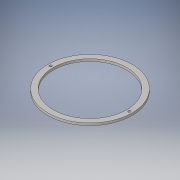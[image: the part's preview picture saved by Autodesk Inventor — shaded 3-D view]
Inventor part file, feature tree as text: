
AUTODESK INVENTOR PART (.ipt)
format: ipt  version: 2016 (Build 200138000, 138)  size: 108,032 bytes
history: native  units: in
note: dims shown in document units (in); Inventor stores cm internally (conversion verified against a paired STEP export)
features: extrude x2, sketch x2
ambient origin geometry x8: Origin, YZ Plane, XZ Plane, XY Plane, X Axis, Y Axis, Z Axis, Center Point
bodies: Solid1 (feature_tree)
feature tree (4):
  extrude  "Extrusion1"  Depth=3.44in
  extrude  "Extrusion2"  Depth=0.11in
  sketch  "Sketch1"  dims[d0=0.25in d1=3.44in]
  sketch  "Sketch2"  dims[d2=0.11in d3=0.0in d4=0.1181in d5=0.1181in d6=1.845in d7=1.845in d8=0.11in d9=0.0in]
